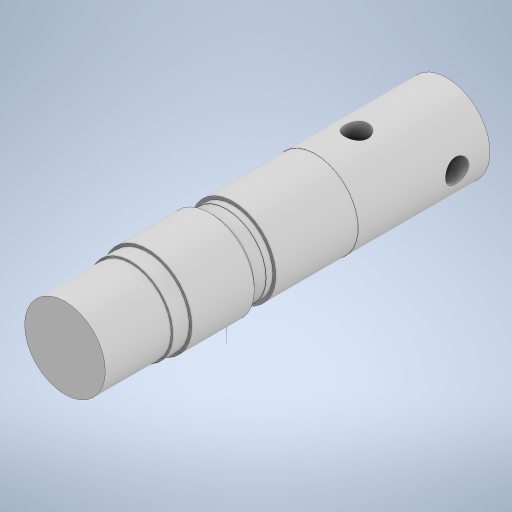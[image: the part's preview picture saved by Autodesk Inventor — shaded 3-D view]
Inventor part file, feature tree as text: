
AUTODESK INVENTOR PART (.ipt)
format: ipt  version: 2024 (Build 280153000, 153)  size: 318,976 bytes
history: native  units: mm
features: sketch x5, extrude x2, plane x1, revolve x1, chamfer x1
ambient origin geometry x8: Origin, YZ Plane, XZ Plane, XY Plane, X Axis, Y Axis, Z Axis, Center Point
bodies: Body1 (feature_tree)
feature tree (10):
  sketch  "Sketch1"  dims[d2=40.0mm d4=8.0mm]
  plane  "Work Plane1"
  sketch  "Sketch3"  dims[d5=4.0mm d6=50.0mm]
  sketch  "Sketch4"  dims[d16=10.0mm d17=15.0mm]
  revolve  "Revolution1"  [1 undecoded]
  extrude  "Extrusion5"  Depth=4.0mm
  extrude  "Extrusion6"  Depth=10.0mm
  chamfer  "Chamfer3"  Angle=90.0deg  [1 undecoded]
  sketch  "Sketch5"  dims[d22=14.0mm]
  sketch  "Sketch6"  dims[d28=14.0mm d31=90.0deg d34=20.0mm d35=45.0mm d36=0.0mm d37=0.0mm d38=35.0mm d39=30.0mm d40=0.0mm d41=0.0mm d48=2.0mm d49=2.0mm d50=45.0deg d66=79.0mm d67=114.0mm d71=27.0mm d78=24.0mm d82=4.0mm d83=50.0mm d84=24.2mm d85=26.1mm d86=80.0mm d88=25.5mm d89=26.0mm d90=40.0mm d92=24.5mm d20=0.5mm d21=0.872665mm d23=0.872665mm d32=0.872665mm]
note: 2 required parameter values undecoded (feature->parameter linkage not recoverable at this tier; creation-order binding heuristic only, values carry confidence <= 0.55)